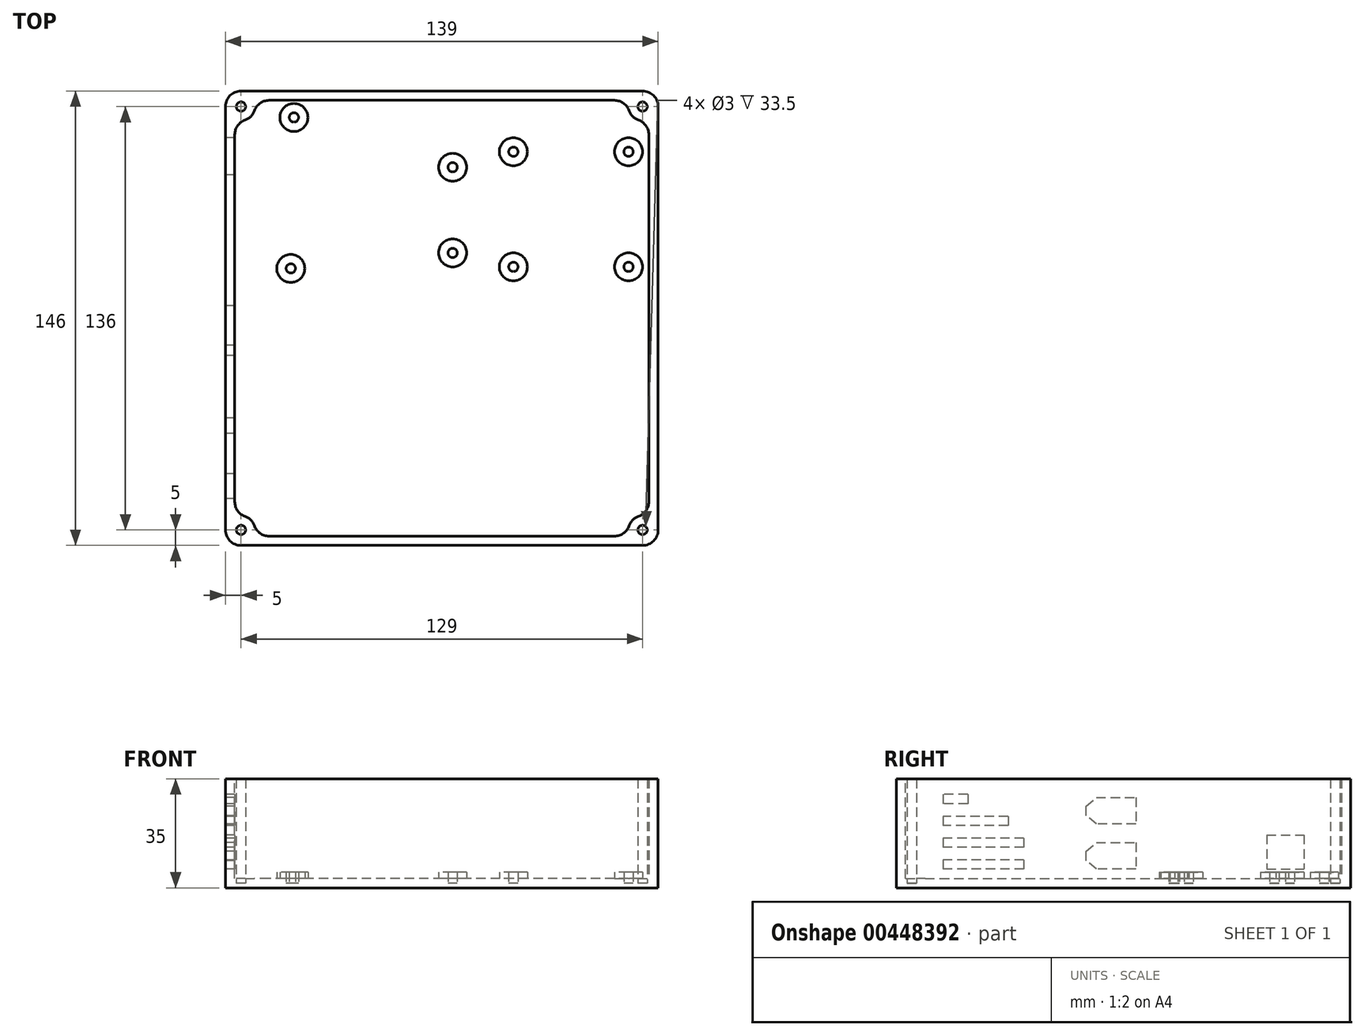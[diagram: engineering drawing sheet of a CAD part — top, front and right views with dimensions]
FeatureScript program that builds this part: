
annotation { "Feature Type Name" : "Feature", "Feature Type Description" : "" }
export const myFeature = defineFeature(function(context is Context, id is Id, definition is map)
    precondition{}
    {
        {
            var Q0;
            Q0=qCreatedBy(makeId("Top.planeOp"),FACE);
            var sketch = newSketch(context, id + "F0", { "sketchPlane" : qUnion([Q0])});
            skLineSegment(sketch, "E0.bottom", {"start": v(66.5, -70) * mm, "end": v(-66.5, -70) * mm});
            skLineSegment(sketch, "E0.top", {"start": v(66.5, 70) * mm, "end": v(-66.5, 70) * mm});
            skLineSegment(sketch, "E0.left", {"start": v(66.5, -70) * mm, "end": v(66.5, 70) * mm});
            skLineSegment(sketch, "E0.right", {"start": v(-66.5, -70) * mm, "end": v(-66.5, 70) * mm});
            skPoint(sketch, "E0.middle", {"position": v(0, 0) * mm});
            skLineSegment(sketch, "E1.bottom", {"start": v(64.5, -73) * mm, "end": v(-64.5, -73) * mm});
            skLineSegment(sketch, "E1.top", {"start": v(64.5, 73) * mm, "end": v(-64.5, 73) * mm});
            skLineSegment(sketch, "E1.left", {"start": v(69.5, -68) * mm, "end": v(69.5, 68) * mm});
            skLineSegment(sketch, "E1.right", {"start": v(-69.5, -68) * mm, "end": v(-69.5, 68) * mm});
            skCircle(sketch, "E2", {"center": v(-47.5, 64.5) * mm, "radius": 4.5 * mm});
            skCircle(sketch, "E3", {"center": v(-48.5, 16) * mm, "radius": 4.5 * mm});
            skCircle(sketch, "E4", {"center": v(3.5, 48.5) * mm, "radius": 4.5 * mm});
            skCircle(sketch, "E5", {"center": v(3.5, 21) * mm, "radius": 4.5 * mm});
            skCircle(sketch, "E6", {"center": v(60, 53.5) * mm, "radius": 4.5 * mm});
            skCircle(sketch, "E7", {"center": v(60, 16.5) * mm, "radius": 4.5 * mm});
            skCircle(sketch, "E8", {"center": v(23, 53.5) * mm, "radius": 4.5 * mm});
            skCircle(sketch, "E9", {"center": v(23, 16.5) * mm, "radius": 4.5 * mm});
            skCircle(sketch, "E10", {"center": v(-47.5, 64.5) * mm, "radius": 1.5 * mm});
            skCircle(sketch, "E11", {"center": v(-48.5, 16) * mm, "radius": 1.5 * mm});
            skCircle(sketch, "E12", {"center": v(3.5, 21) * mm, "radius": 1.5 * mm});
            skCircle(sketch, "E13", {"center": v(3.5, 48.5) * mm, "radius": 1.5 * mm});
            skCircle(sketch, "E14", {"center": v(23, 53.5) * mm, "radius": 1.5 * mm});
            skCircle(sketch, "E15", {"center": v(23, 16.5) * mm, "radius": 1.5 * mm});
            skCircle(sketch, "E16", {"center": v(60, 16.5) * mm, "radius": 1.5 * mm});
            skCircle(sketch, "E17", {"center": v(60, 53.5) * mm, "radius": 1.5 * mm});
            skLineSegment(sketch, "E18.bottom", {"start": v(-66.5, 46) * mm, "end": v(-69.5, 46) * mm});
            skLineSegment(sketch, "E18.top", {"start": v(-66.5, 58) * mm, "end": v(-69.5, 58) * mm});
            skLineSegment(sketch, "E18.left", {"start": v(-66.5, 46) * mm, "end": v(-66.5, 58) * mm});
            skLineSegment(sketch, "E18.right", {"start": v(-69.5, 46) * mm, "end": v(-69.5, 58) * mm});
            skPoint(sketch, "E18.middle", {"position": v(-68, 52) * mm});
            skCircle(sketch, "E19", {"center": v(-64.5, 68) * mm, "radius": 4.5 * mm});
            skCircle(sketch, "E20", {"center": v(-64.5, -68) * mm, "radius": 4.5 * mm});
            skCircle(sketch, "E21", {"center": v(-64.5, 68) * mm, "radius": 1.5 * mm});
            skCircle(sketch, "E22", {"center": v(64.5, 68) * mm, "radius": 4.5 * mm});
            skCircle(sketch, "E23", {"center": v(64.5, 68) * mm, "radius": 1.5 * mm});
            skCircle(sketch, "E24", {"center": v(64.5, -68) * mm, "radius": 4.5 * mm});
            skCircle(sketch, "E25", {"center": v(64.5, -68) * mm, "radius": 1.5 * mm});
            skCircle(sketch, "E26", {"center": v(-64.5, -68) * mm, "radius": 1.5 * mm});
            skPoint(sketch, "E27.visualSharp", {"position": v(-69.5, -73) * mm});
            skArc(sketch, "E27.filletArc", {"start": v(-69.5, -68) * mm, "mid": v(-68.04, -71.54) * mm, "end": v(-64.5, -73) * mm});
            skPoint(sketch, "E28.visualSharp", {"position": v(-69.5, 73) * mm});
            skArc(sketch, "E28.filletArc", {"start": v(-64.5, 73) * mm, "mid": v(-68.04, 71.54) * mm, "end": v(-69.5, 68) * mm});
            skPoint(sketch, "E29.visualSharp", {"position": v(69.5, 73) * mm});
            skArc(sketch, "E29.filletArc", {"start": v(69.5, 68) * mm, "mid": v(68.04, 71.54) * mm, "end": v(64.5, 73) * mm});
            skPoint(sketch, "E30.visualSharp", {"position": v(69.5, -73) * mm});
            skArc(sketch, "E30.filletArc", {"start": v(64.5, -73) * mm, "mid": v(68.04, -71.54) * mm, "end": v(69.5, -68) * mm});
            skSolve(sketch);
        }
        {
            var Q0;
            {var subQ3=sQuery(id+"F0.wireOp",EDGE,"E0.bottom");Q0=makeQuery(id+"F0.imprint","IMPRINT",FACE,{"disambiguationData":[TD([[makeQuery(id+"F0.imprint","IMPRINT",EDGE,{"derivedFrom":subQ3}),-1.0]])]});}
            var Q1;
            Q1=makeQuery(id+"F0.imprint","IMPRINT",FACE,{"disambiguationData":[TD([[makeQuery(id+"F0.imprint","IMPRINT",EDGE,{"derivedFrom":sQuery(id+"F0.wireOp",EDGE,"E2")}),-1.0]])]});
            var Q2;
            Q2=makeQuery(id+"F0.imprint","IMPRINT",FACE,{"disambiguationData":[TD([[makeQuery(id+"F0.imprint","IMPRINT",EDGE,{"derivedFrom":sQuery(id+"F0.wireOp",EDGE,"E23")}),-1.0]])]});
            var Q3;
            Q3=makeQuery(id+"F0.imprint","IMPRINT",FACE,{"disambiguationData":[TD([[makeQuery(id+"F0.imprint","IMPRINT",EDGE,{"derivedFrom":sQuery(id+"F0.wireOp",EDGE,"E21")}),-1.0]])]});
            extrude(context, id + "F1", {"entities" : qUnion([Q0, Q1, Q2, Q3]), "depth" : 3 * mm});
        }
        {
            var Q0;
            Q0=makeQuery(id+"F0.imprint","IMPRINT",FACE,{"disambiguationData":[TD([[makeQuery(id+"F0.imprint","IMPRINT",EDGE,{"derivedFrom":sQuery(id+"F0.wireOp",EDGE,"E2")}),1.0]])]});
            var Q1;
            Q1=makeQuery(id+"F0.imprint","IMPRINT",FACE,{"disambiguationData":[TD([[makeQuery(id+"F0.imprint","IMPRINT",EDGE,{"derivedFrom":sQuery(id+"F0.wireOp",EDGE,"E3")}),1.0]])]});
            var Q2;
            Q2=makeQuery(id+"F0.imprint","IMPRINT",FACE,{"disambiguationData":[TD([[makeQuery(id+"F0.imprint","IMPRINT",EDGE,{"derivedFrom":sQuery(id+"F0.wireOp",EDGE,"E4")}),1.0]])]});
            var Q3;
            Q3=makeQuery(id+"F0.imprint","IMPRINT",FACE,{"disambiguationData":[TD([[makeQuery(id+"F0.imprint","IMPRINT",EDGE,{"derivedFrom":sQuery(id+"F0.wireOp",EDGE,"E8")}),1.0]])]});
            var Q4;
            Q4=makeQuery(id+"F0.imprint","IMPRINT",FACE,{"disambiguationData":[TD([[makeQuery(id+"F0.imprint","IMPRINT",EDGE,{"derivedFrom":sQuery(id+"F0.wireOp",EDGE,"E9")}),1.0]])]});
            var Q5;
            Q5=makeQuery(id+"F0.imprint","IMPRINT",FACE,{"disambiguationData":[TD([[makeQuery(id+"F0.imprint","IMPRINT",EDGE,{"derivedFrom":sQuery(id+"F0.wireOp",EDGE,"E6")}),1.0]])]});
            var Q6;
            Q6=makeQuery(id+"F0.imprint","IMPRINT",FACE,{"disambiguationData":[TD([[makeQuery(id+"F0.imprint","IMPRINT",EDGE,{"derivedFrom":sQuery(id+"F0.wireOp",EDGE,"E7")}),1.0]])]});
            var Q7;
            Q7=makeQuery(id+"F0.imprint","IMPRINT",FACE,{"disambiguationData":[TD([[makeQuery(id+"F0.imprint","IMPRINT",EDGE,{"derivedFrom":sQuery(id+"F0.wireOp",EDGE,"E5")}),1.0]])]});
            extrude(context, id + "F2", {"entities" : qUnion([Q0, Q1, Q2, Q3, Q4, Q5, Q6, Q7]), "operationType" : NewBodyOperationType.ADD, "depth" : 5 * mm});
        }
        {
            var Q0;
            Q0=makeQuery(id+"F0.imprint","IMPRINT",FACE,{"disambiguationData":[TD([[makeQuery(id+"F0.imprint","IMPRINT",EDGE,{"derivedFrom":sQuery(id+"F0.wireOp",EDGE,"E10")}),1.0]])]});
            var Q1;
            Q1=makeQuery(id+"F0.imprint","IMPRINT",FACE,{"disambiguationData":[TD([[makeQuery(id+"F0.imprint","IMPRINT",EDGE,{"derivedFrom":sQuery(id+"F0.wireOp",EDGE,"E11")}),1.0]])]});
            var Q2;
            Q2=makeQuery(id+"F0.imprint","IMPRINT",FACE,{"disambiguationData":[TD([[makeQuery(id+"F0.imprint","IMPRINT",EDGE,{"derivedFrom":sQuery(id+"F0.wireOp",EDGE,"E13")}),1.0]])]});
            var Q3;
            Q3=makeQuery(id+"F0.imprint","IMPRINT",FACE,{"disambiguationData":[TD([[makeQuery(id+"F0.imprint","IMPRINT",EDGE,{"derivedFrom":sQuery(id+"F0.wireOp",EDGE,"E12")}),1.0]])]});
            var Q4;
            Q4=makeQuery(id+"F0.imprint","IMPRINT",FACE,{"disambiguationData":[TD([[makeQuery(id+"F0.imprint","IMPRINT",EDGE,{"derivedFrom":sQuery(id+"F0.wireOp",EDGE,"E14")}),1.0]])]});
            var Q5;
            Q5=makeQuery(id+"F0.imprint","IMPRINT",FACE,{"disambiguationData":[TD([[makeQuery(id+"F0.imprint","IMPRINT",EDGE,{"derivedFrom":sQuery(id+"F0.wireOp",EDGE,"E15")}),1.0]])]});
            var Q6;
            Q6=makeQuery(id+"F0.imprint","IMPRINT",FACE,{"disambiguationData":[TD([[makeQuery(id+"F0.imprint","IMPRINT",EDGE,{"derivedFrom":sQuery(id+"F0.wireOp",EDGE,"E16")}),1.0]])]});
            var Q7;
            Q7=makeQuery(id+"F0.imprint","IMPRINT",FACE,{"disambiguationData":[TD([[makeQuery(id+"F0.imprint","IMPRINT",EDGE,{"derivedFrom":sQuery(id+"F0.wireOp",EDGE,"E17")}),1.0]])]});
            var Q8;
            Q8=makeQuery(id+"F0.imprint","IMPRINT",FACE,{"disambiguationData":[TD([[makeQuery(id+"F0.imprint","IMPRINT",EDGE,{"derivedFrom":sQuery(id+"F0.wireOp",EDGE,"E26")}),1.0]])]});
            var Q9;
            Q9=makeQuery(id+"F0.imprint","IMPRINT",FACE,{"disambiguationData":[TD([[makeQuery(id+"F0.imprint","IMPRINT",EDGE,{"derivedFrom":sQuery(id+"F0.wireOp",EDGE,"E25")}),1.0]])]});
            var Q10;
            Q10=makeQuery(id+"F0.imprint","IMPRINT",FACE,{"disambiguationData":[TD([[makeQuery(id+"F0.imprint","IMPRINT",EDGE,{"derivedFrom":sQuery(id+"F0.wireOp",EDGE,"E23")}),1.0]])]});
            var Q11;
            Q11=makeQuery(id+"F0.imprint","IMPRINT",FACE,{"disambiguationData":[TD([[makeQuery(id+"F0.imprint","IMPRINT",EDGE,{"derivedFrom":sQuery(id+"F0.wireOp",EDGE,"E21")}),1.0]])]});
            extrude(context, id + "F3", {"entities" : qUnion([Q0, Q1, Q2, Q3, Q4, Q5, Q6, Q7, Q8, Q9, Q10, Q11]), "operationType" : NewBodyOperationType.ADD, "depth" : 1.5 * mm});
        }
        {
            var Q0;
            {var subQ9=sQuery(id+"F0.wireOp",EDGE,"E0.bottom");Q0=makeQuery(id+"F0.imprint","IMPRINT",FACE,{"disambiguationData":[TD([[makeQuery(id+"F0.imprint","IMPRINT",EDGE,{"derivedFrom":subQ9}),1.0]])]});}
            var Q1;
            Q1=makeQuery(id+"F0.imprint","IMPRINT",FACE,{"disambiguationData":[TD([[makeQuery(id+"F0.imprint","IMPRINT",EDGE,{"derivedFrom":sQuery(id+"F0.wireOp",EDGE,"E1.bottom")}),-1.0]])]});
            var Q2;
            {var subQ0=sQuery(id+"F0.wireOp",EDGE,"E0.right");var subQ1=sQuery(id+"F0.wireOp",EDGE,"E0.top");var subQ2=makeQuery(id+"F0.imprint","INTERSECT",VERTEX,{"derivedFrom":[subQ1,subQ0]});Q2=makeQuery(id+"F0.imprint","IMPRINT",FACE,{"disambiguationData":[TD([[makeQuery(id+"F0.imprint","IMPRINT",EDGE,{"disambiguationData":[TD([[subQ2,1.0]])],"derivedFrom":subQ1}),-1.0]])]});}
            var Q3;
            {var subQ0=sQuery(id+"F0.wireOp",EDGE,"E0.left");var subQ1=sQuery(id+"F0.wireOp",EDGE,"E0.top");var subQ2=makeQuery(id+"F0.imprint","INTERSECT",VERTEX,{"derivedFrom":[subQ1,subQ0]});Q3=makeQuery(id+"F0.imprint","IMPRINT",FACE,{"disambiguationData":[TD([[makeQuery(id+"F0.imprint","IMPRINT",EDGE,{"disambiguationData":[TD([[subQ2,-1.0]])],"derivedFrom":subQ1}),-1.0]])]});}
            var Q4;
            Q4=makeQuery(id+"F0.imprint","IMPRINT",FACE,{"disambiguationData":[TD([[makeQuery(id+"F0.imprint","IMPRINT",EDGE,{"derivedFrom":sQuery(id+"F0.wireOp",EDGE,"E23")}),-1.0]])]});
            var Q5;
            Q5=makeQuery(id+"F0.imprint","IMPRINT",FACE,{"disambiguationData":[TD([[makeQuery(id+"F0.imprint","IMPRINT",EDGE,{"derivedFrom":sQuery(id+"F0.wireOp",EDGE,"E25")}),-1.0]])]});
            var Q6;
            Q6=makeQuery(id+"F0.imprint","IMPRINT",FACE,{"disambiguationData":[TD([[makeQuery(id+"F0.imprint","IMPRINT",EDGE,{"derivedFrom":sQuery(id+"F0.wireOp",EDGE,"E21")}),-1.0]])]});
            var Q7;
            Q7=makeQuery(id+"F0.imprint","IMPRINT",FACE,{"disambiguationData":[TD([[makeQuery(id+"F0.imprint","IMPRINT",EDGE,{"derivedFrom":sQuery(id+"F0.wireOp",EDGE,"E26")}),-1.0]])]});
            extrude(context, id + "F4", {"entities" : qUnion([Q0, Q1, Q2, Q3, Q4, Q5, Q6, Q7]), "operationType" : NewBodyOperationType.ADD, "depth" : 35 * mm});
        }
        {
            var Q0;
            Q0=makeQuery(id+"F0.imprint","IMPRINT",FACE,{"disambiguationData":[TD([[makeQuery(id+"F0.imprint","IMPRINT",EDGE,{"derivedFrom":sQuery(id+"F0.wireOp",EDGE,"E18.bottom")}),-1.0]])]});
            extrude(context, id + "F5", {"entities" : qUnion([Q0]), "operationType" : NewBodyOperationType.ADD, "depth" : 6 * mm});
        }
        {
            var Q0;
            Q0=makeQuery(id+"F4.opExtrude","SWEPT_EDGE",EDGE,{"disambiguationData":[OSD([sQuery(id+"F0.wireOp",EDGE,"E0.top"),sQuery(id+"F0.wireOp",EDGE,"E22")])]});
            var Q1;
            Q1=makeQuery(id+"F4.opExtrude","SWEPT_EDGE",EDGE,{"disambiguationData":[OSD([sQuery(id+"F0.wireOp",EDGE,"E0.left"),sQuery(id+"F0.wireOp",EDGE,"E22")])]});
            var Q2;
            Q2=makeQuery(id+"F4.opExtrude","SWEPT_EDGE",EDGE,{"disambiguationData":[OSD([sQuery(id+"F0.wireOp",EDGE,"E0.top"),sQuery(id+"F0.wireOp",EDGE,"E19")])]});
            var Q3;
            Q3=makeQuery(id+"F4.opExtrude","SWEPT_EDGE",EDGE,{"disambiguationData":[OSD([sQuery(id+"F0.wireOp",EDGE,"E0.right"),sQuery(id+"F0.wireOp",EDGE,"E19")])]});
            var Q4;
            Q4=makeQuery(id+"F4.opExtrude","SWEPT_EDGE",EDGE,{"disambiguationData":[OSD([sQuery(id+"F0.wireOp",EDGE,"E0.right"),sQuery(id+"F0.wireOp",EDGE,"E20")])]});
            var Q5;
            Q5=makeQuery(id+"F4.opExtrude","SWEPT_EDGE",EDGE,{"disambiguationData":[OSD([sQuery(id+"F0.wireOp",EDGE,"E0.bottom"),sQuery(id+"F0.wireOp",EDGE,"E20")])]});
            var Q6;
            Q6=makeQuery(id+"F4.opExtrude","SWEPT_EDGE",EDGE,{"disambiguationData":[OSD([sQuery(id+"F0.wireOp",EDGE,"E0.left"),sQuery(id+"F0.wireOp",EDGE,"E24")])]});
            var Q7;
            Q7=makeQuery(id+"F4.opExtrude","SWEPT_EDGE",EDGE,{"disambiguationData":[OSD([sQuery(id+"F0.wireOp",EDGE,"E0.bottom"),sQuery(id+"F0.wireOp",EDGE,"E24")])]});
            fillet(context, id + "F6", {"entities" : qUnion([Q0, Q1, Q2, Q3, Q4, Q5, Q6, Q7]), "radius" : 5 * mm, "tangentPropagation" : true, "allowEdgeOverflow" : false});
        }
        {
            var Q0;
            Q0=makeQuery(id+"F0.imprint","IMPRINT",FACE,{"disambiguationData":[TD([[makeQuery(id+"F0.imprint","IMPRINT",EDGE,{"derivedFrom":sQuery(id+"F0.wireOp",EDGE,"E18.bottom")}),-1.0]])]});
            extrude(context, id + "F7", {"entities" : qUnion([Q0]), "operationType" : NewBodyOperationType.ADD, "depth" : 35 * mm, "hasSecondDirection" : true, "secondDirectionOppositeDirection" : true, "secondDirectionDepth" : -17 * mm});
        }
        {
            var Q0;
            {var subQ0=sQuery(id+"F0.wireOp",EDGE,"E18.right");var subQ1=sQuery(id+"F0.wireOp",EDGE,"E1.right");Q0=makeQuery(id+"F7.boolean.opBoolean","MERGE",FACE,{"derivedFrom":[makeQuery(id+"F5.boolean.opBoolean","MERGE",FACE,{"derivedFrom":[makeQuery(id+"F4.opExtrude","SWEPT_FACE",FACE,{"disambiguationData":[OSD([subQ1]),TDD([makeQuery(id+"F0.imprint","IMPRINT",EDGE,{"disambiguationData":[TD([[makeQuery(id+"F0.imprint","INTERSECT",VERTEX,{"derivedFrom":[subQ1,sQuery(id+"F0.wireOp",EDGE,"E27.filletArc")]}),-1.0]])],"derivedFrom":subQ1})])]}),makeQuery(id+"F4.opExtrude","SWEPT_FACE",FACE,{"disambiguationData":[OSD([subQ1]),TDD([makeQuery(id+"F0.imprint","IMPRINT",EDGE,{"disambiguationData":[TD([[makeQuery(id+"F0.imprint","INTERSECT",VERTEX,{"derivedFrom":[subQ1,sQuery(id+"F0.wireOp",EDGE,"E28.filletArc")]}),1.0]])],"derivedFrom":subQ1})])]}),makeQuery(id+"F5.opExtrude","SWEPT_FACE",FACE,{"disambiguationData":[OSD([subQ0])]})]}),makeQuery(id+"F7.opExtrude","SWEPT_FACE",FACE,{"disambiguationData":[OSD([subQ0])]})]});}
            cPlane(context, id + "F8", {"entities" : qUnion([Q0]), "cplaneType" : CPlaneType.OFFSET, "offset" : 25 * mm, "width" : 150 * mm, "height" : 150 * mm});
        }
        {
            var Q0;
            Q0=qCreatedBy(id+"F8.planeOp",FACE);
            var sketch = newSketch(context, id + "F9", { "sketchPlane" : qUnion([Q0])});
            skLineSegment(sketch, "E31.bottom", {"start": v(32, 16) * mm, "end": v(58, 16) * mm});
            skLineSegment(sketch, "E31.top", {"start": v(32, 13) * mm, "end": v(58, 13) * mm});
            skLineSegment(sketch, "E31.left", {"start": v(32, 16) * mm, "end": v(32, 13) * mm});
            skLineSegment(sketch, "E31.right", {"start": v(58, 16) * mm, "end": v(58, 13) * mm});
            skLineSegment(sketch, "E32.bottom", {"start": v(32, 9) * mm, "end": v(58, 9) * mm});
            skLineSegment(sketch, "E32.top", {"start": v(32, 6) * mm, "end": v(58, 6) * mm});
            skLineSegment(sketch, "E32.left", {"start": v(32, 9) * mm, "end": v(32, 6) * mm});
            skLineSegment(sketch, "E32.right", {"start": v(58, 9) * mm, "end": v(58, 6) * mm});
            skLineSegment(sketch, "E33.bottom", {"start": v(37, 23) * mm, "end": v(58, 23) * mm});
            skLineSegment(sketch, "E33.top", {"start": v(37, 20) * mm, "end": v(58, 20) * mm});
            skLineSegment(sketch, "E33.left", {"start": v(37, 23) * mm, "end": v(37, 20) * mm});
            skLineSegment(sketch, "E33.right", {"start": v(58, 23) * mm, "end": v(58, 20) * mm});
            skLineSegment(sketch, "E34.bottom", {"start": v(50, 30) * mm, "end": v(58, 30) * mm});
            skLineSegment(sketch, "E34.top", {"start": v(50, 27) * mm, "end": v(58, 27) * mm});
            skLineSegment(sketch, "E34.left", {"start": v(50, 30) * mm, "end": v(50, 27) * mm});
            skLineSegment(sketch, "E34.right", {"start": v(58, 30) * mm, "end": v(58, 27) * mm});
            skLineSegment(sketch, "E35", {"start": v(-4, 14.5) * mm, "end": v(-4, 6) * mm});
            skLineSegment(sketch, "E36", {"start": v(-4, 6) * mm, "end": v(8.7, 6) * mm});
            skLineSegment(sketch, "E37", {"start": v(8.7, 6) * mm, "end": v(12, 8.75) * mm});
            skLineSegment(sketch, "E38", {"start": v(12, 8.75) * mm, "end": v(12, 11.75) * mm});
            skLineSegment(sketch, "E39", {"start": v(12, 11.75) * mm, "end": v(8.7, 14.5) * mm});
            skLineSegment(sketch, "E40", {"start": v(8.7, 14.5) * mm, "end": v(-4, 14.5) * mm});
            skLineSegment(sketch, "E41", {"start": v(-4, 29) * mm, "end": v(-4, 20.5) * mm});
            skLineSegment(sketch, "E42", {"start": v(-4, 20.5) * mm, "end": v(8.7, 20.5) * mm});
            skLineSegment(sketch, "E43", {"start": v(8.7, 20.5) * mm, "end": v(12, 23.25) * mm});
            skLineSegment(sketch, "E44", {"start": v(12, 23.25) * mm, "end": v(12, 26.25) * mm});
            skLineSegment(sketch, "E45", {"start": v(12, 26.25) * mm, "end": v(8.7, 29) * mm});
            skLineSegment(sketch, "E46", {"start": v(8.7, 29) * mm, "end": v(-4, 29) * mm});
            skSolve(sketch);
        }
        {
            var Q0;
            Q0=makeQuery(id+"F9.imprint","IMPRINT",FACE,{"disambiguationData":[TD([[makeQuery(id+"F9.imprint","IMPRINT",EDGE,{"derivedFrom":sQuery(id+"F9.wireOp",EDGE,"E34.bottom")}),-1.0]])]});
            var Q1;
            Q1=makeQuery(id+"F9.imprint","IMPRINT",FACE,{"disambiguationData":[TD([[makeQuery(id+"F9.imprint","IMPRINT",EDGE,{"derivedFrom":sQuery(id+"F9.wireOp",EDGE,"E33.bottom")}),-1.0]])]});
            var Q2;
            Q2=makeQuery(id+"F9.imprint","IMPRINT",FACE,{"disambiguationData":[TD([[makeQuery(id+"F9.imprint","IMPRINT",EDGE,{"derivedFrom":sQuery(id+"F9.wireOp",EDGE,"E31.bottom")}),-1.0]])]});
            var Q3;
            Q3=makeQuery(id+"F9.imprint","IMPRINT",FACE,{"disambiguationData":[TD([[makeQuery(id+"F9.imprint","IMPRINT",EDGE,{"derivedFrom":sQuery(id+"F9.wireOp",EDGE,"E32.bottom")}),-1.0]])]});
            var Q4;
            Q4=makeQuery(id+"F9.imprint","IMPRINT",FACE,{"disambiguationData":[TD([[makeQuery(id+"F9.imprint","IMPRINT",EDGE,{"derivedFrom":sQuery(id+"F9.wireOp",EDGE,"E35")}),1.0]])]});
            var Q5;
            Q5=makeQuery(id+"F9.imprint","IMPRINT",FACE,{"disambiguationData":[TD([[makeQuery(id+"F9.imprint","IMPRINT",EDGE,{"derivedFrom":sQuery(id+"F9.wireOp",EDGE,"E41")}),1.0]])]});
            extrude(context, id + "F10", {"entities" : qUnion([Q0, Q1, Q2, Q3, Q4, Q5]), "operationType" : NewBodyOperationType.REMOVE, "oppositeDirection" : true, "depth" : 28 * mm});
        }
    });
